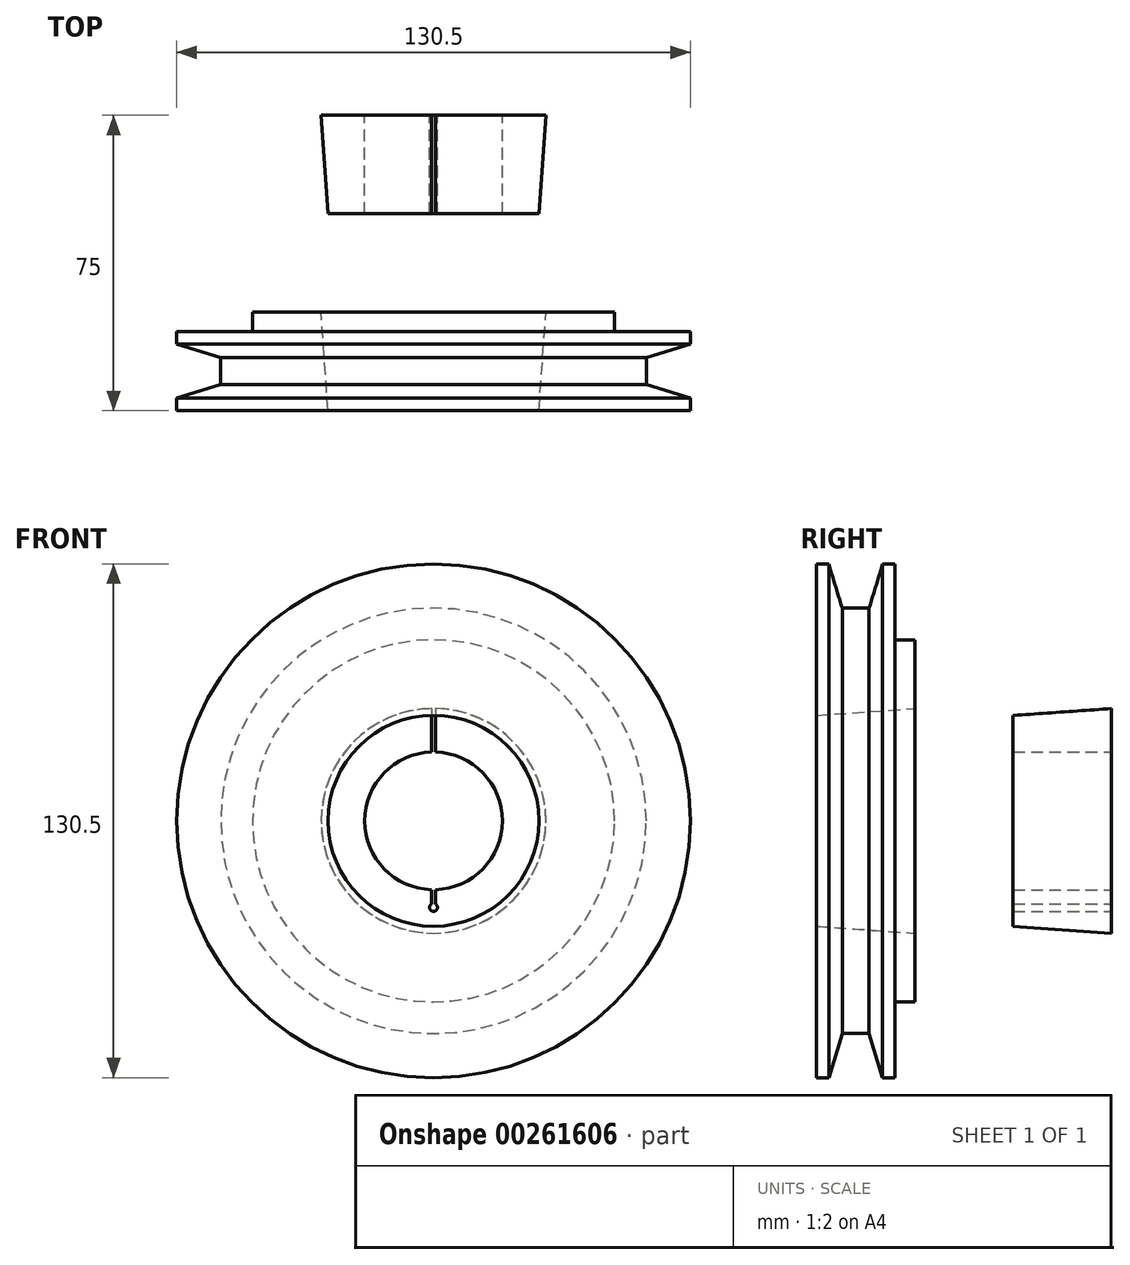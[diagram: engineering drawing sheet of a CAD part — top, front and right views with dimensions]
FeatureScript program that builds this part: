
annotation { "Feature Type Name" : "Feature", "Feature Type Description" : "" }
export const myFeature = defineFeature(function(context is Context, id is Id, definition is map)
    precondition{}
    {
        {
            var Q0;
            Q0=qCreatedBy(makeId("Right.planeOp"),FACE);
            var sketch = newSketch(context, id + "F0", { "sketchPlane" : qUnion([Q0]), "disableImprinting" : false});
            skLineSegment(sketch, "E0", {"start": v(0, 0) * mm, "end": v(0, 65.25) * mm});
            skLineSegment(sketch, "E1", {"start": v(20, 65.25) * mm, "end": v(20, 46) * mm});
            skLineSegment(sketch, "E2", {"start": v(20, 46) * mm, "end": v(25, 46) * mm});
            skLineSegment(sketch, "E3", {"start": v(25, 46) * mm, "end": v(25, 0) * mm});
            skLineSegment(sketch, "E4", {"start": v(25, 0) * mm, "end": v(0, 0) * mm});
            skLineSegment(sketch, "E5", {"start": v(0, 65.25) * mm, "end": v(3.15, 65.25) * mm});
            skLineSegment(sketch, "E6", {"start": v(3.15, 65.25) * mm, "end": v(6.57, 54.05) * mm});
            skLineSegment(sketch, "E7", {"start": v(6.57, 54.05) * mm, "end": v(13.43, 54.05) * mm});
            skLineSegment(sketch, "E8", {"start": v(13.43, 54.05) * mm, "end": v(16.85, 65.25) * mm});
            skLineSegment(sketch, "E9", {"start": v(16.85, 65.25) * mm, "end": v(20, 65.25) * mm});
            skSolve(sketch);
        }
        {
            var Q0;
            Q0=makeQuery(id+"F0.imprint","IMPRINT",FACE,{"disambiguationData":[TD([[makeQuery(id+"F0.imprint","IMPRINT",EDGE,{"derivedFrom":sQuery(id+"F0.wireOp",EDGE,"E0")}),-1.0]])]});
            var Q1;
            Q1=sQuery(id+"F0.wireOp",EDGE,"E4");
            revolve(context, id + "F1", {"entities" : qUnion([Q0]), "axis" : qUnion([Q1]), "revolveType" : RevolveType.FULL});
        }
        {
            var Q0;
            Q0=makeQuery(id+"F1.opRevolve","SWEPT_FACE",FACE,{"disambiguationData":[OSD([sQuery(id+"F0.wireOp",EDGE,"E0")])]});
            var sketch = newSketch(context, id + "F2", { "sketchPlane" : qUnion([Q0])});
            skCircle(sketch, "E10", {"center": v(0, 0) * mm, "radius": 26.8 * mm});
            skSolve(sketch);
        }
        {
            var Q0;
            Q0=qSketchRegion(id+"F2",true);
            extrude(context, id + "F3", {"entities" : qUnion([Q0]), "operationType" : NewBodyOperationType.REMOVE, "oppositeDirection" : true, "depth" : 25 * mm, "hasDraft" : true, "draftAngle" : 4 * degree});
        }
        {
            var Q0;
            Q0=makeQuery(id+"F1.opRevolve","SWEPT_FACE",FACE,{"disambiguationData":[OSD([sQuery(id+"F0.wireOp",EDGE,"E3")])]});
            cPlane(context, id + "F4", {"entities" : qUnion([Q0]), "cplaneType" : CPlaneType.OFFSET, "offset" : 25 * mm, "width" : 150 * mm, "height" : 150 * mm});
        }
        {
            var Q0;
            Q0=qCreatedBy(id+"F4.planeOp",FACE);
            var sketch = newSketch(context, id + "F5", { "sketchPlane" : qUnion([Q0])});
            skCircle(sketch, "E11", {"center": v(0, 0) * mm, "radius": 26.79 * mm});
            skSolve(sketch);
        }
        {
            var Q0;
            Q0=qSketchRegion(id+"F5",true);
            extrude(context, id + "F6", {"entities" : qUnion([Q0]), "depth" : 25 * mm, "hasDraft" : true, "draftAngle" : 4 * degree});
        }
        {
            var Q0;
            Q0=makeQuery(id+"F6.opExtrude","CAP_FACE",FACE,{"disambiguationData":[OSD([sQuery(id+"F5.wireOp",EDGE,"E11")])],"isStart":false});
            var sketch = newSketch(context, id + "F7", { "sketchPlane" : qUnion([Q0])});
            skCircle(sketch, "E12", {"center": v(0, 0) * mm, "radius": 17.5 * mm});
            skSolve(sketch);
        }
        {
            var Q0;
            Q0=qSketchRegion(id+"F7",true);
            var Q1;
            Q1=makeQuery(id+"F6.opExtrude","CAP_FACE",FACE,{"disambiguationData":[OSD([sQuery(id+"F5.wireOp",EDGE,"E11")])],"isStart":true});
            extrude(context, id + "F8", {"entities" : qUnion([Q0]), "operationType" : NewBodyOperationType.REMOVE, "endBound" : BoundingType.UP_TO_SURFACE, "oppositeDirection" : true, "endBoundEntityFace" : qUnion([Q1]), "depth" : 25 * mm});
        }
        {
            var Q0;
            Q0=makeQuery(id+"F6.opExtrude","CAP_FACE",FACE,{"disambiguationData":[OSD([sQuery(id+"F5.wireOp",EDGE,"E11")])],"isStart":false});
            var sketch = newSketch(context, id + "F9", { "sketchPlane" : qUnion([Q0])});
            skLineSegment(sketch, "E13.bottom", {"start": v(0.5, 30) * mm, "end": v(-0.5, 30) * mm});
            skLineSegment(sketch, "E13.top", {"start": v(0.5, -22) * mm, "end": v(-0.5, -22) * mm});
            skLineSegment(sketch, "E13.left", {"start": v(0.5, 30) * mm, "end": v(0.5, -22) * mm});
            skLineSegment(sketch, "E13.right", {"start": v(-0.5, 30) * mm, "end": v(-0.5, -22) * mm});
            skPoint(sketch, "E13.middle", {"position": v(0, 4) * mm});
            skCircle(sketch, "E14", {"center": v(0, -22) * mm, "radius": 1 * mm});
            skSolve(sketch);
        }
        {
            var Q0;
            Q0=qSketchRegion(id+"F9",true);
            var Q1;
            Q1=makeQuery(id+"F6.opExtrude","CAP_FACE",FACE,{"disambiguationData":[OSD([sQuery(id+"F5.wireOp",EDGE,"E11")])],"isStart":true});
            extrude(context, id + "F10", {"entities" : qUnion([Q0]), "operationType" : NewBodyOperationType.REMOVE, "endBound" : BoundingType.UP_TO_SURFACE, "oppositeDirection" : true, "endBoundEntityFace" : qUnion([Q1]), "depth" : 25 * mm});
        }
    });
